# Revit family: GL
name_source: partatom
category: Mechanical Equipment
units: mm (PartAtom-declared; Revit-internal decimal feet)

## family parameters
Always vertical = Yes
Cut with Voids When Loaded = No
Part Type = Normal
Room Calculation Point = No
Round Connector Dimension = Use Diameter
Shared = No
Work Plane-Based = No

## types (6) — shared parameters
Copper Pipes = Copper
DEPTH = 28 3/4"
Description = 3-Fan 2-Way Blow Evaporator
HEIGHT = 18 1/4"
Manufacturer = Krack Corporation
Revit Family Dates = 03/02/22SV
Type Comments = GL Series 3-Fan 2-Way Blow Evaporator
URL = www.krack.com

## per-type parameters (varying)
| type | 1 FAN | 2 FAN | 3 FAN | 4 FAN | 5 FAN | 6 FAN | LENGTH |
| GL4 | No | No | No | Yes | No | No | 85 3/4" |
| GL3 | No | No | Yes | No | No | No | 67 3/4" |
| GL2 | No | Yes | No | No | No | No | 49 3/4" |
| GL1 | Yes | No | No | No | No | No | 31 3/4" |
| GL5 | No | No | No | No | Yes | No | 103 3/4" |
| GL6 | No | No | No | No | No | Yes | 121 3/4" |

note: column(s) folded — value = type name in every type: Model

## geometry (parser evidence)
native form markers: Sweep x17
no freeform markers — native parametric forms only
